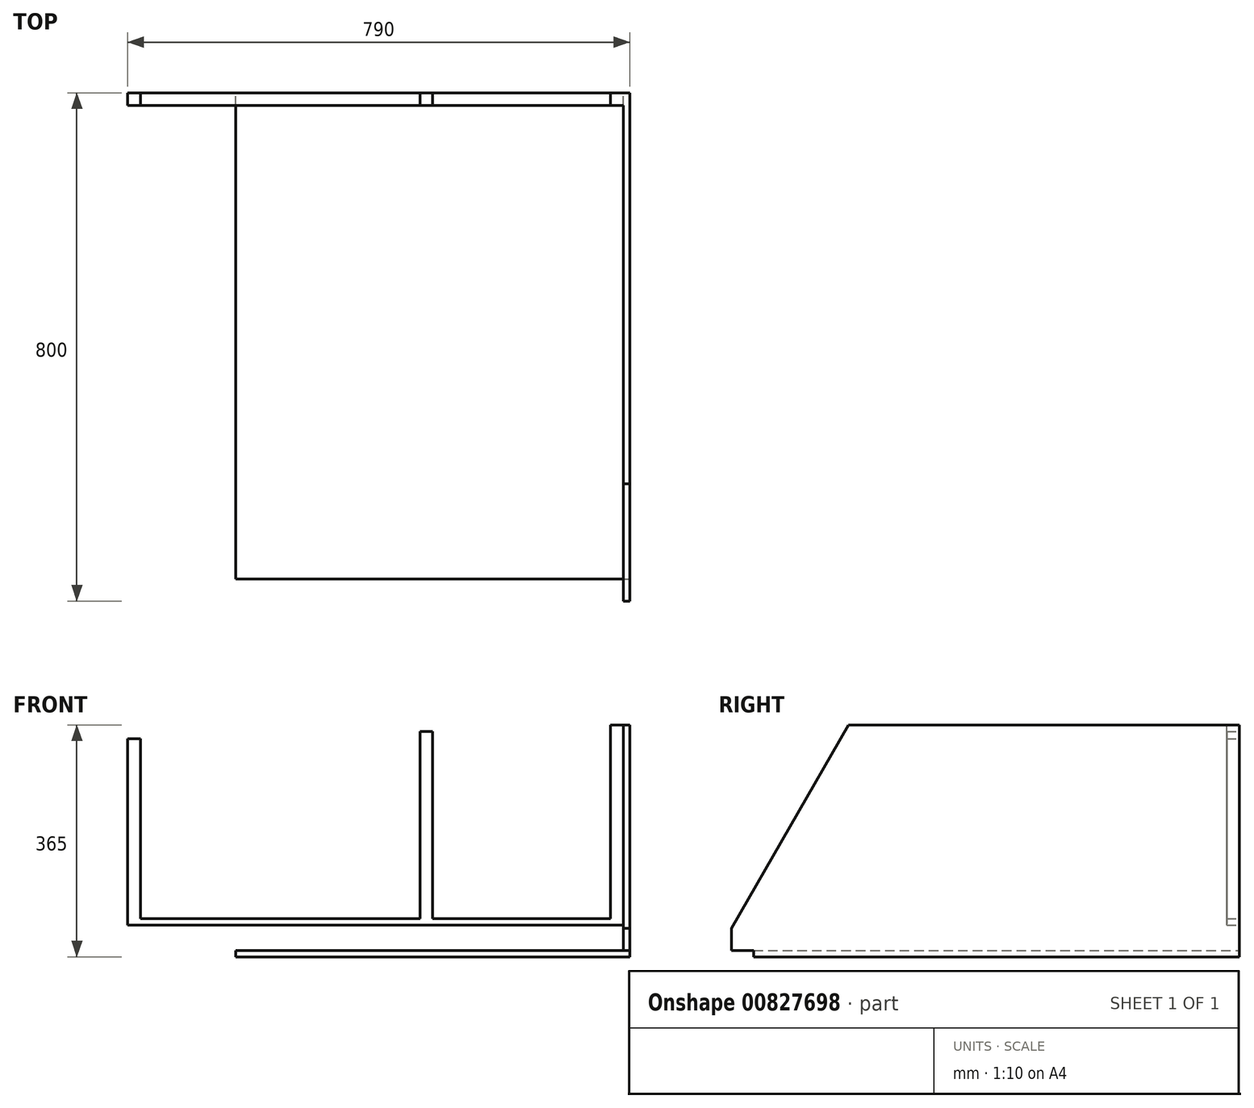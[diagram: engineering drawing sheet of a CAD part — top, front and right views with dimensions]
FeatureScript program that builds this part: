
annotation { "Feature Type Name" : "Feature", "Feature Type Description" : "" }
export const myFeature = defineFeature(function(context is Context, id is Id, definition is map)
    precondition{}
    {
        {
            var Q0;
            Q0=qCreatedBy(makeId("Front.planeOp"),FACE);
            var sketch = newSketch(context, id + "F0", { "sketchPlane" : qUnion([Q0])});
            skLineSegment(sketch, "E0", {"start": v(0, 0) * mm, "end": v(780, 0) * mm});
            skLineSegment(sketch, "E1", {"start": v(780, 0) * mm, "end": v(780, 315) * mm});
            skLineSegment(sketch, "E2", {"start": v(0, 293) * mm, "end": v(0, 0) * mm});
            skLineSegment(sketch, "E3", {"start": v(0, 293) * mm, "end": v(20, 293) * mm});
            skLineSegment(sketch, "E4", {"start": v(20, 293) * mm, "end": v(20, 10) * mm});
            skLineSegment(sketch, "E5", {"start": v(20, 10) * mm, "end": v(460, 10) * mm});
            skLineSegment(sketch, "E6", {"start": v(460, 10) * mm, "end": v(460, 305) * mm});
            skLineSegment(sketch, "E7", {"start": v(460, 305) * mm, "end": v(480, 305) * mm});
            skLineSegment(sketch, "E8", {"start": v(480, 305) * mm, "end": v(480, 10) * mm});
            skLineSegment(sketch, "E9", {"start": v(480, 10) * mm, "end": v(760, 10) * mm});
            skLineSegment(sketch, "E10", {"start": v(760, 10) * mm, "end": v(760, 315) * mm});
            skLineSegment(sketch, "E11", {"start": v(760, 315) * mm, "end": v(780, 315) * mm});
            skSolve(sketch);
        }
        {
            var Q0;
            Q0=makeQuery(id+"F0.imprint","IMPRINT",FACE,{"disambiguationData":[TD([[makeQuery(id+"F0.imprint","IMPRINT",EDGE,{"derivedFrom":sQuery(id+"F0.wireOp",EDGE,"E0")}),1.0]])]});
            extrude(context, id + "F1", {"entities" : qUnion([Q0]), "depth" : 20 * mm, "offsetDistance" : 25 * mm});
        }
        {
            var Q0;
            Q0=makeQuery(id+"F1.opExtrude","SWEPT_FACE",FACE,{"disambiguationData":[OSD([sQuery(id+"F0.wireOp",EDGE,"E1")])]});
            var sketch = newSketch(context, id + "F2", { "sketchPlane" : qUnion([Q0])});
            skLineSegment(sketch, "E12.top", {"start": v(0, 315) * mm, "end": v(-800, 315) * mm});
            skLineSegment(sketch, "E12.right", {"start": v(-800, -40) * mm, "end": v(-800, 315) * mm});
            skLineSegment(sketch, "E13", {"start": v(-800, -40) * mm, "end": v(0, -40) * mm});
            skLineSegment(sketch, "E14", {"start": v(0, -40) * mm, "end": v(0, 315) * mm});
            skSolve(sketch);
        }
        {
            var Q0;
            {var subQ2=sQuery(id+"F2.wireOp",EDGE,"E12.right");Q0=makeQuery(id+"F2.imprint","IMPRINT",FACE,{"disambiguationData":[TD([[makeQuery(id+"F2.imprint","IMPRINT",EDGE,{"derivedFrom":subQ2}),-1.0]])]});}
            var Q1;
            {var subQ3=sQuery(id+"F0.wireOp",EDGE,"E1");var subQ4=makeQuery(id+"F1.opExtrude","CAP_EDGE",EDGE,{"disambiguationData":[OSD([subQ3])],"isStart":false});Q1=makeQuery(id+"F2.imprint","IMPRINT",FACE,{"disambiguationData":[TD([[makeQuery(id+"F2.imprint","IMPRINT",EDGE,{"derivedFrom":subQ4}),-1.0]])]});}
            extrude(context, id + "F3", {"entities" : qUnion([Q0, Q1]), "operationType" : NewBodyOperationType.ADD, "depth" : 10 * mm, "offsetDistance" : 25 * mm});
        }
        {
            var Q0;
            Q0=makeQuery(id+"F3.opExtrude","SWEPT_EDGE",EDGE,{"disambiguationData":[OSD([sQuery(id+"F2.wireOp",EDGE,"E12.top"),sQuery(id+"F2.wireOp",EDGE,"E12.right")])]});
            chamfer(context, id + "F4", {"entities" : qUnion([Q0]), "chamferType" : ChamferType.OFFSET_ANGLE, "width" : 320 * mm, "oppositeDirection" : false, "angle" : 30 * degree, "tangentPropagation" : true});
        }
        {
            var Q0;
            Q0=makeQuery(id+"F3.opExtrude","SWEPT_FACE",FACE,{"disambiguationData":[OSD([sQuery(id+"F2.wireOp",EDGE,"E13")])]});
            var sketch = newSketch(context, id + "F5", { "sketchPlane" : qUnion([Q0])});
            skLineSegment(sketch, "E15.bottom", {"start": v(170, 765) * mm, "end": v(790, 765) * mm});
            skLineSegment(sketch, "E15.top", {"start": v(170, 0) * mm, "end": v(790, 0) * mm});
            skLineSegment(sketch, "E15.left", {"start": v(170, 765) * mm, "end": v(170, 0) * mm});
            skLineSegment(sketch, "E15.right", {"start": v(790, 765) * mm, "end": v(790, 0) * mm});
            skSolve(sketch);
        }
        {
            var Q0;
            {var subQ0=sQuery(id+"F5.wireOp",EDGE,"E15.left");Q0=makeQuery(id+"F5.imprint","IMPRINT",FACE,{"disambiguationData":[TD([[makeQuery(id+"F5.imprint","IMPRINT",EDGE,{"derivedFrom":subQ0}),1.0]])]});}
            var Q1;
            {var subQ0=sQuery(id+"F5.wireOp",EDGE,"E15.right");Q1=makeQuery(id+"F5.imprint","IMPRINT",FACE,{"disambiguationData":[TD([[makeQuery(id+"F5.imprint","IMPRINT",EDGE,{"derivedFrom":subQ0}),-1.0]])]});}
            extrude(context, id + "F6", {"entities" : qUnion([Q0, Q1]), "operationType" : NewBodyOperationType.ADD, "depth" : 10 * mm, "offsetDistance" : 25 * mm});
        }
    });
